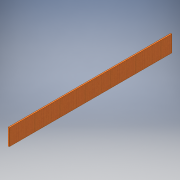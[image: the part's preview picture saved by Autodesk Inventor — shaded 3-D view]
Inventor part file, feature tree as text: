
AUTODESK INVENTOR PART (.ipt)
format: ipt  version: 2016 (Build 200138000, 138)  size: 94,720 bytes
history: native  units: in
note: dims shown in document units (in); Inventor stores cm internally (conversion verified against a paired STEP export)
features: extrude x1, sketch x1
ambient origin geometry x8: Origin, YZ Plane, XZ Plane, XY Plane, X Axis, Y Axis, Z Axis, Center Point
bodies: Solid1 (feature_tree)
feature tree (2):
  extrude  "Extrusion1"  Depth=6.5in
  sketch  "Sketch1"  dims[d0=64.4375in d1=6.5in d2=0.4375in d3=0.0in]
